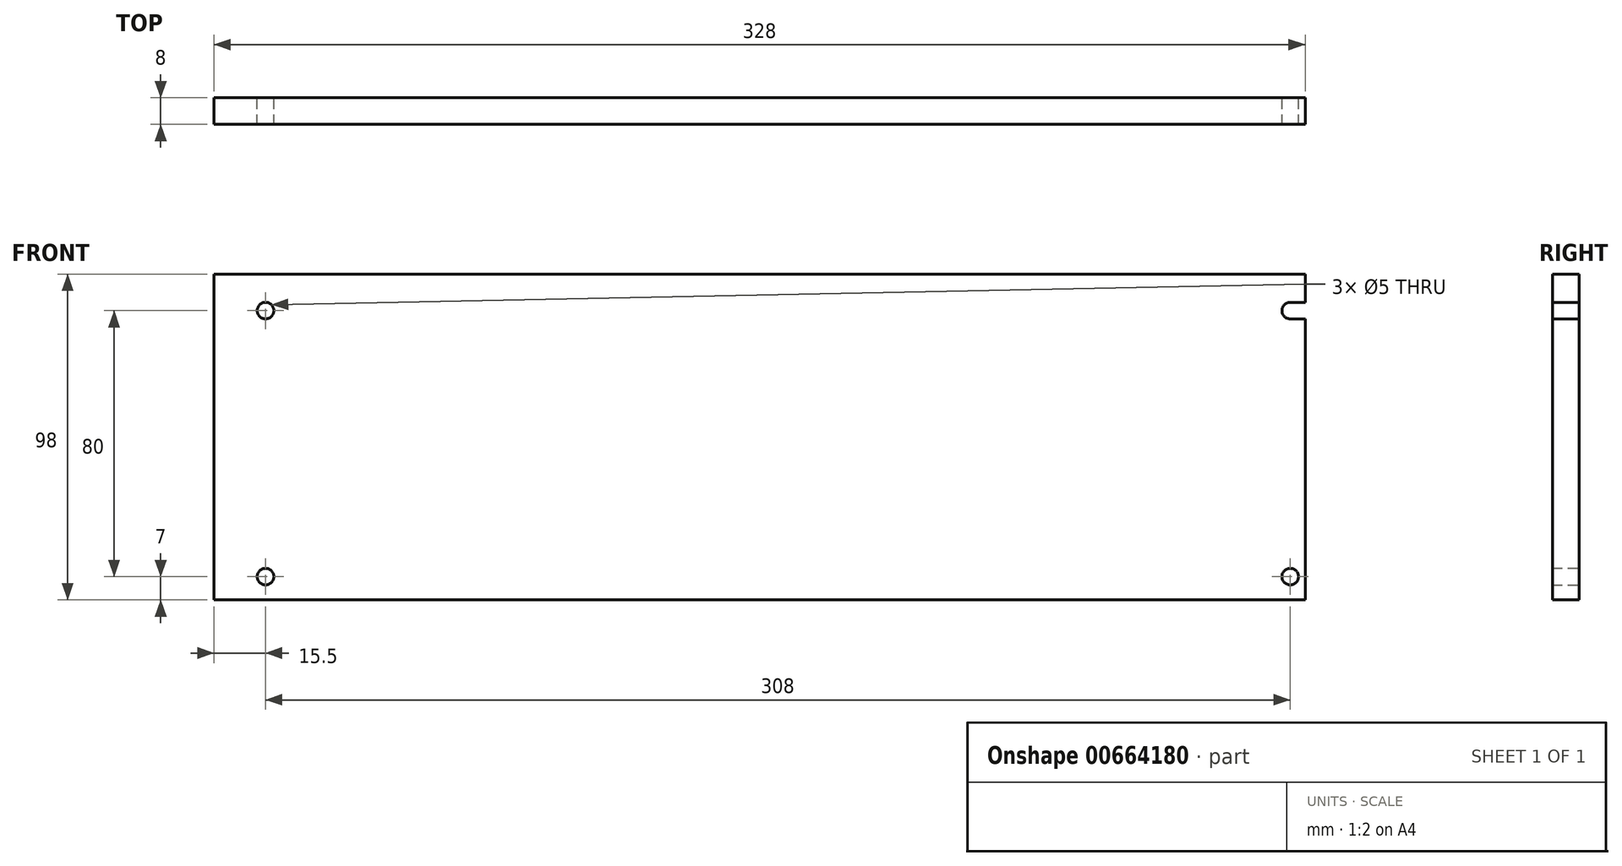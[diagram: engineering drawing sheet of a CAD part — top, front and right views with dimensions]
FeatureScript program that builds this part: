
annotation { "Feature Type Name" : "Feature", "Feature Type Description" : "" }
export const myFeature = defineFeature(function(context is Context, id is Id, definition is map)
    precondition{}
    {
        {
            assignVariable(context, id + "F0", {"name" : "Q38BDepth", "anyValue" : 8});
        }
        {
            var Q0;
            Q0=qCreatedBy(makeId("Front.planeOp"),FACE);
            var sketch = newSketch(context, id + "F1", { "sketchPlane" : qUnion([Q0])});
            skLineSegment(sketch, "E0.bottom", {"start": v(-164, 49) * mm, "end": v(164, 49) * mm});
            skLineSegment(sketch, "E0.top", {"start": v(-164, -49) * mm, "end": v(164, -49) * mm});
            skLineSegment(sketch, "E0.left", {"start": v(-164, 49) * mm, "end": v(-164, -49) * mm});
            skLineSegment(sketch, "E0.right", {"start": v(164, 49) * mm, "end": v(164, -49) * mm});
            skCircle(sketch, "E1", {"center": v(159.5, 38) * mm, "radius": 2.5 * mm});
            skLineSegment(sketch, "E2", {"start": v(159.5, 40.5) * mm, "end": v(164, 40.5) * mm});
            skLineSegment(sketch, "E3", {"start": v(159.5, 35.5) * mm, "end": v(164, 35.5) * mm});
            skCircle(sketch, "E4", {"center": v(159.5, -42) * mm, "radius": 2.5 * mm});
            skCircle(sketch, "E5", {"center": v(-148.5, -42) * mm, "radius": 2.5 * mm});
            skCircle(sketch, "E6", {"center": v(-148.5, 38) * mm, "radius": 2.5 * mm});
            skSolve(sketch);
        }
        {
            var Q0;
            Q0=makeQuery(id+"F1.imprint","IMPRINT",FACE,{"disambiguationData":[TD([[makeQuery(id+"F1.imprint","IMPRINT",EDGE,{"derivedFrom":sQuery(id+"F1.wireOp",EDGE,"E0.bottom")}),-1.0]])]});
            extrude(context, id + "F2", {"entities" : qUnion([Q0]), "depth" : (getVariable(context, 'Q38BDepth')) * mm});
        }
    });
